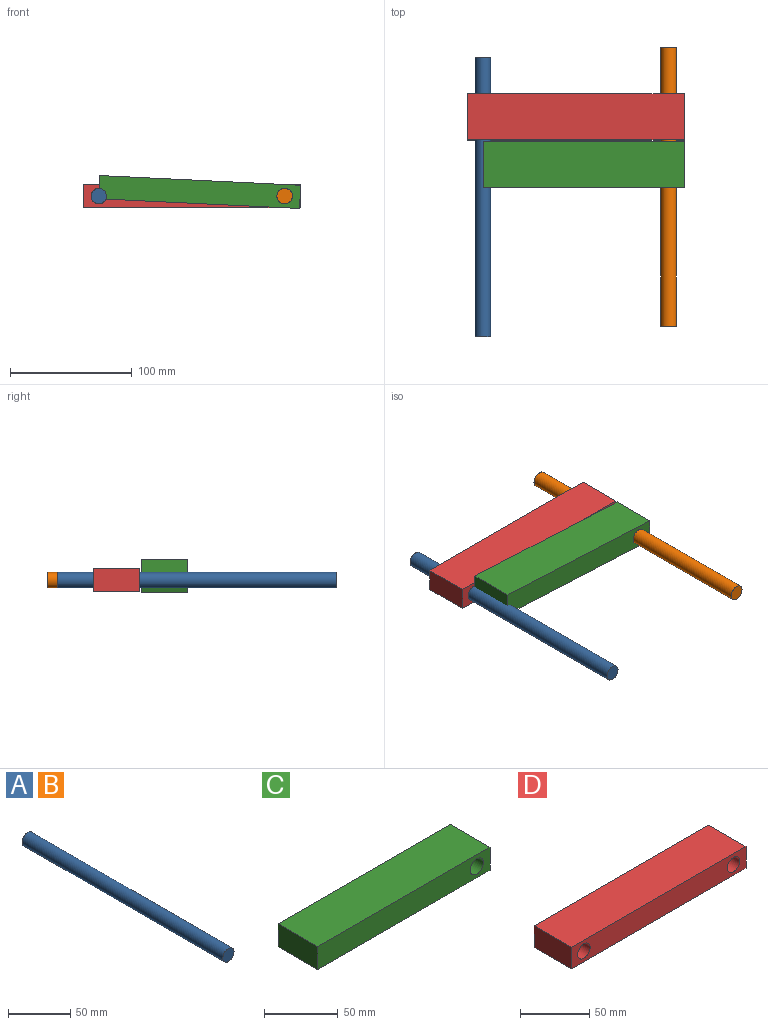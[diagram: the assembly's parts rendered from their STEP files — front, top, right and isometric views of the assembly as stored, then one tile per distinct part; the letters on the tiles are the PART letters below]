
ASSEMBLY  parts=4 mates=3
PART A: 3 faces, bbox 12.7x228.6x12.7 mm
  f0: cylinder r=6.35mm len=228.6mm, axis (0,-1,0), area 9120.7mm2, adj f1,f2
  f1: plane 12.7x12.7mm, normal (0,1,0), area 126.7mm2, adj f0
  f2: plane 12.7x12.7mm, normal (0,-1,0), area 126.7mm2, adj f0
PART B: same geometry as A
PART C: 7 faces, bbox 165.1x38.1x19.1 mm
  f0: plane 38.1x19.05mm, normal (-1,0,0), area 725.8mm2, adj f1,f3,f4,f5
  f1: plane 165.1x19.05mm, normal (0,-1,0), area 3018.5mm2, adj f0,f2,f4,f5,f6
  f2: plane 38.1x19.05mm, normal (1,0,0), area 725.8mm2, adj f1,f3,f4,f5
  f3: plane 165.1x19.05mm, normal (0,1,0), area 3018.5mm2, adj f0,f2,f4,f5,f6
  f4: plane 165.1x38.1mm, normal (0,0,1), area 6290.3mm2, adj f0,f1,f2,f3
  f5: plane 165.1x38.1mm, normal (0,0,-1), area 6290.3mm2, adj f0,f1,f2,f3
  f6: cylinder r=6.35mm len=38.1mm, axis (0,-1,0), area 1520.1mm2, adj f1,f3
PART D: 8 faces, bbox 177.8x38.1x19.1 mm
  f0: plane 38.1x19.05mm, normal (-1,0,0), area 725.8mm2, adj f1,f3,f4,f5
  f1: plane 177.8x19.05mm, normal (0,-1,0), area 3133.7mm2, adj f0,f2,f4,f5,f6,f7
  f2: plane 38.1x19.05mm, normal (1,0,0), area 725.8mm2, adj f1,f3,f4,f5
  f3: plane 177.8x19.05mm, normal (0,1,0), area 3133.7mm2, adj f0,f2,f4,f5,f6,f7
  f4: plane 177.8x38.1mm, normal (0,0,1), area 6774.2mm2, adj f0,f1,f2,f3
  f5: plane 177.8x38.1mm, normal (0,0,-1), area 6774.2mm2, adj f0,f1,f2,f3
  f6: cylinder r=6.35mm len=38.1mm, axis (0,-1,0), area 1520.1mm2, adj f1,f3
  f7: cylinder r=6.35mm len=38.1mm, axis (0,-1,0), area 1520.1mm2, adj f1,f3
PLACE A rot(axis=(0,1,0),35.8deg) t=(36.35,-101.86,42.93)mm
PLACE B rot(axis=(0,-1,0),1.1deg) t=(188.75,-93.28,42.93)mm
PLACE C rot(axis=(0,1,0),2.8deg) t=(36.07,20.3,40.79)mm
PLACE D t=(23.65,59.39,33.4)mm fixed
MATE cylindrical A.f0 <-> D.f6  axis (0,-1,0) through (36.35,-101.86,42.93)mm
MATE cylindrical C.f6 <-> B.f0  axis (0,-1,0) through (188.75,20.3,42.93)mm
MATE cylindrical B.f0 <-> D.f7  axis (0,-1,0) through (188.75,135.32,42.93)mm
